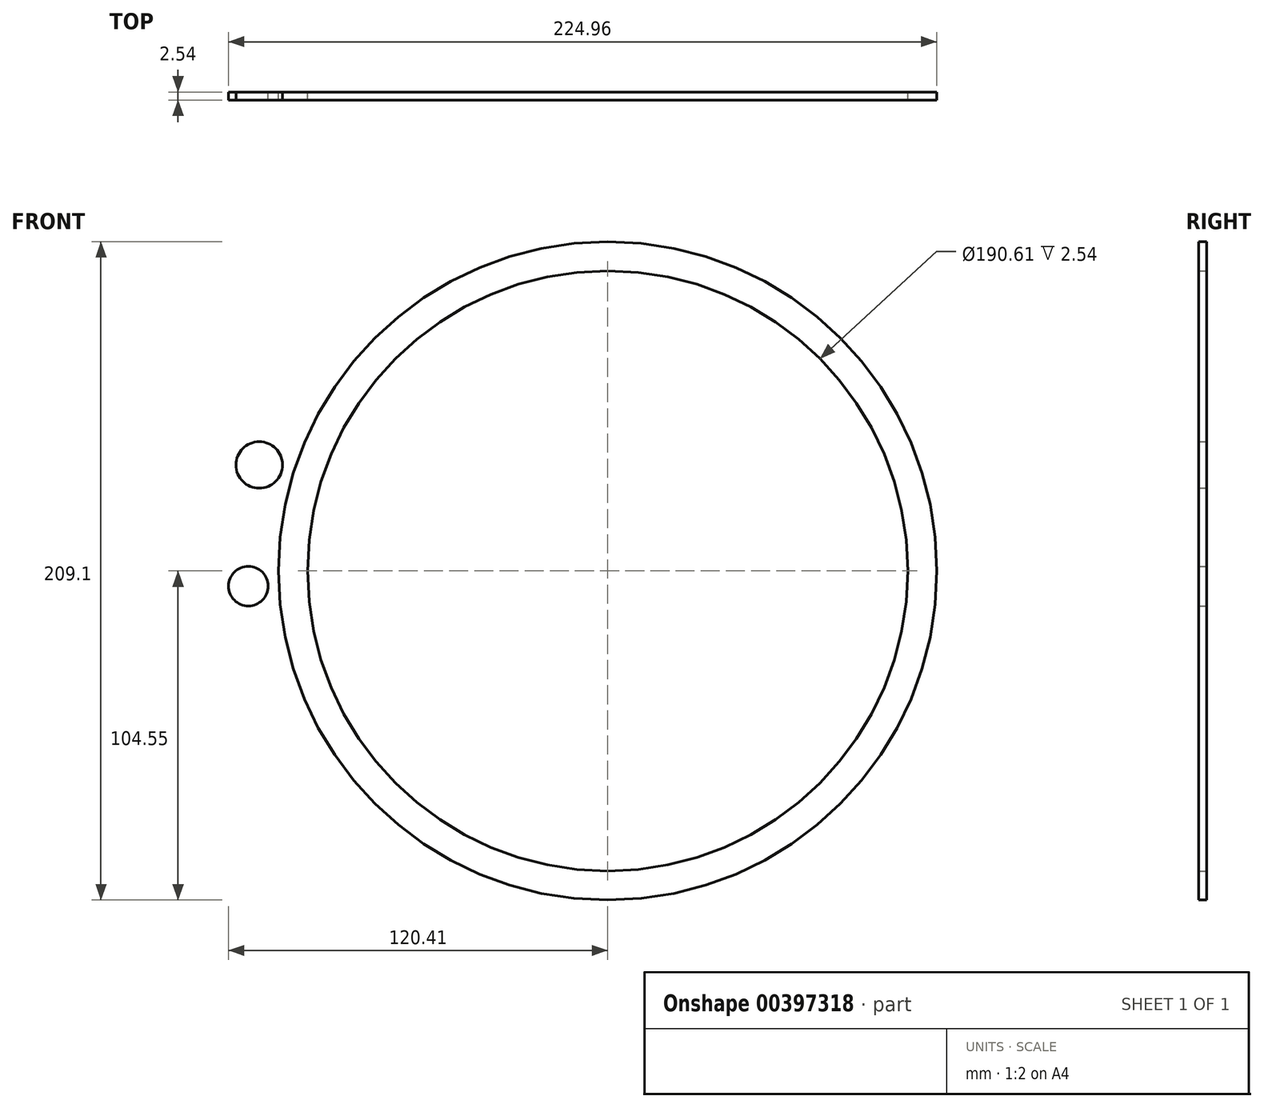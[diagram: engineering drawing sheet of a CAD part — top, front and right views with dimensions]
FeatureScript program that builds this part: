
annotation { "Feature Type Name" : "Feature", "Feature Type Description" : "" }
export const myFeature = defineFeature(function(context is Context, id is Id, definition is map)
    precondition{}
    {
        {
            var Q0;
            Q0=qCreatedBy(makeId("Front.planeOp"),FACE);
            var sketch = newSketch(context, id + "F0", { "sketchPlane" : qUnion([Q0])});
            skCircle(sketch, "E0", {"center": v(0, 0) * mm, "radius": 104.55 * mm});
            skCircle(sketch, "E1", {"center": v(0, 0) * mm, "radius": 95.3 * mm});
            skCircle(sketch, "E2", {"center": v(0, 0) * mm, "radius": 89.92 * mm});
            skCircle(sketch, "E3", {"center": v(0, 0) * mm, "radius": 84.79 * mm});
            skCircle(sketch, "E4", {"center": v(0, 0) * mm, "radius": 81.45 * mm});
            skCircle(sketch, "E5", {"center": v(0, 0) * mm, "radius": 77.92 * mm});
            skCircle(sketch, "E6", {"center": v(0, 0) * mm, "radius": 74.78 * mm});
            skCircle(sketch, "E7", {"center": v(0, 0) * mm, "radius": 72.87 * mm});
            skCircle(sketch, "E8", {"center": v(0, 0) * mm, "radius": 70.75 * mm});
            skCircle(sketch, "E9", {"center": v(0, 0) * mm, "radius": 68.27 * mm});
            skCircle(sketch, "E10", {"center": v(0, 0) * mm, "radius": 65.38 * mm});
            skCircle(sketch, "E11", {"center": v(0, 0) * mm, "radius": 63.36 * mm});
            skCircle(sketch, "E12", {"center": v(0, 0) * mm, "radius": 62 * mm});
            skCircle(sketch, "E13", {"center": v(0, 0) * mm, "radius": 61 * mm});
            skCircle(sketch, "E14", {"center": v(0, 0) * mm, "radius": 59.24 * mm});
            skCircle(sketch, "E15", {"center": v(0, 0) * mm, "radius": 55.27 * mm});
            skCircle(sketch, "E16", {"center": v(0, 0) * mm, "radius": 51.1 * mm});
            skCircle(sketch, "E17", {"center": v(0, 0) * mm, "radius": 45 * mm});
            skCircle(sketch, "E18", {"center": v(0, 0) * mm, "radius": 41.95 * mm});
            skCircle(sketch, "E19", {"center": v(0, 0) * mm, "radius": 38.13 * mm});
            skCircle(sketch, "E20", {"center": v(0, 0) * mm, "radius": 35.24 * mm});
            skCircle(sketch, "E21", {"center": v(0, 0) * mm, "radius": 33.26 * mm});
            skCircle(sketch, "E22", {"center": v(0, 0) * mm, "radius": 31.07 * mm});
            skCircle(sketch, "E23", {"center": v(0, 0) * mm, "radius": 28.45 * mm});
            skCircle(sketch, "E24", {"center": v(0, 0) * mm, "radius": 26.23 * mm});
            skCircle(sketch, "E25", {"center": v(0, 0) * mm, "radius": 24.18 * mm});
            skCircle(sketch, "E26", {"center": v(0, 0) * mm, "radius": 20.17 * mm});
            skCircle(sketch, "E27", {"center": v(0, 0) * mm, "radius": 22 * mm});
            skCircle(sketch, "E28", {"center": v(0, 0) * mm, "radius": 17.11 * mm});
            skCircle(sketch, "E29", {"center": v(0, 0) * mm, "radius": 18.21 * mm});
            skCircle(sketch, "E30", {"center": v(0, 3.15) * mm, "radius": 3.15 * mm});
            skCircle(sketch, "E31", {"center": v(0, 0) * mm, "radius": 13.72 * mm});
            skCircle(sketch, "E32", {"center": v(0, 0) * mm, "radius": 11.1 * mm});
            skCircle(sketch, "E33", {"center": v(0, 0) * mm, "radius": 8.48 * mm});
            skCircle(sketch, "E34", {"center": v(0, 0) * mm, "radius": 7.1 * mm});
            skSolve(sketch);
        }
        {
            var Q0;
            Q0=makeQuery(id+"F0.imprint","IMPRINT",FACE,{"disambiguationData":[TD([[makeQuery(id+"F0.imprint","IMPRINT",EDGE,{"derivedFrom":sQuery(id+"F0.wireOp",EDGE,"E0")}),1.0]])]});
            extrude(context, id + "F1", {"entities" : qUnion([Q0]), "depth" : 2.54 * mm});
        }
        {
            var Q0;
            Q0=qCreatedBy(makeId("Front.planeOp"),FACE);
            var sketch = newSketch(context, id + "F2", { "sketchPlane" : qUnion([Q0])});
            skSolve(sketch);
        }
        {
            var Q0;
            Q0=qCreatedBy(makeId("Front.planeOp"),FACE);
            var sketch = newSketch(context, id + "F3", { "sketchPlane" : qUnion([Q0])});
            skCircle(sketch, "E35", {"center": v(-94, 7.17) * mm, "radius": 45.46 * mm});
            skCircle(sketch, "E36", {"center": v(-110.65, 33.63) * mm, "radius": 7.38 * mm});
            skCircle(sketch, "E37", {"center": v(-114.1, -4.85) * mm, "radius": 6.3 * mm});
            skSolve(sketch);
        }
        {
            var Q0;
            Q0=makeQuery(id+"F3.imprint","IMPRINT",FACE,{"disambiguationData":[TD([[makeQuery(id+"F3.imprint","IMPRINT",EDGE,{"derivedFrom":sQuery(id+"F3.wireOp",EDGE,"E36")}),1.0]])]});
            extrude(context, id + "F4", {"entities" : qUnion([Q0]), "depth" : 2.54 * mm});
        }
        {
            var Q0;
            Q0 = qSketchRegion(id + "F2", true);
            var Q1;
            Q1=makeQuery(id+"F3.imprint","IMPRINT",FACE,{"disambiguationData":[TD([[makeQuery(id+"F3.imprint","IMPRINT",EDGE,{"derivedFrom":sQuery(id+"F3.wireOp",EDGE,"E37")}),1.0]])]});
            extrude(context, id + "F5", {"entities" : qUnion([Q0, Q1]), "depth" : 2.54 * mm});
        }
        {
            var Q0;
            Q0=makeQuery(id+"F3.imprint","IMPRINT",FACE,{"disambiguationData":[TD([[makeQuery(id+"F3.imprint","IMPRINT",EDGE,{"derivedFrom":sQuery(id+"F3.wireOp",EDGE,"E35")}),1.0]])]});
            var sketch = newSketch(context, id + "F6", { "sketchPlane" : qUnion([Q0])});
            skCircle(sketch, "E38", {"center": v(-85.66, 12.6) * mm, "radius": 6.95 * mm});
            skSolve(sketch);
        }
        {
            var Q0;
            Q0=sQuery(id+"F6.wireOp",EDGE,"E38");
            extrude(context, id + "F7", {"bodyType" : ToolBodyType.SURFACE, "surfaceEntities" : qUnion([Q0]), "depth" : 2.54 * mm});
        }
    });
